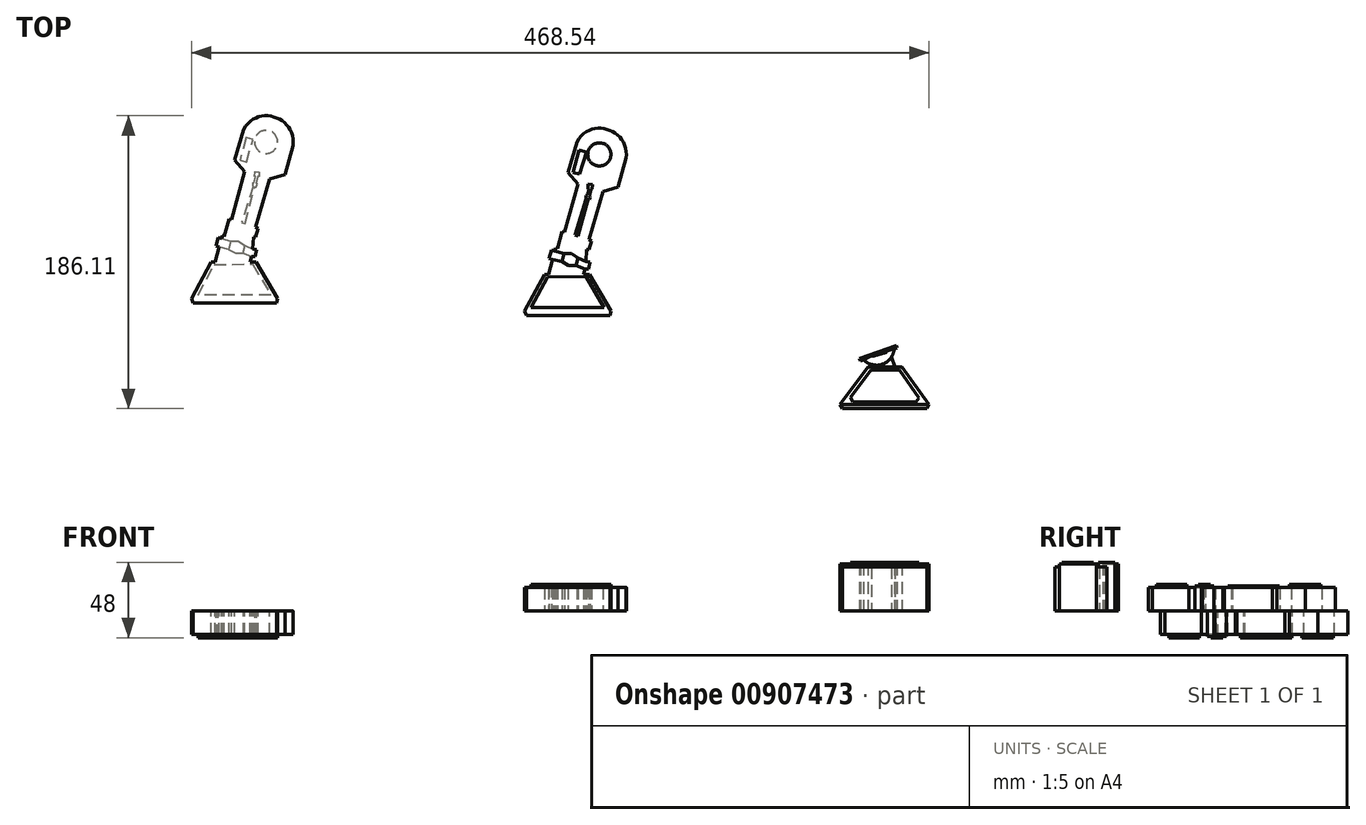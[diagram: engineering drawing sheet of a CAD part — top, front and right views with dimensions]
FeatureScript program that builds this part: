
annotation { "Feature Type Name" : "Feature", "Feature Type Description" : "" }
export const myFeature = defineFeature(function(context is Context, id is Id, definition is map)
    precondition{}
    {
        {
            var Q0;
            Q0=qCreatedBy(makeId("Top.planeOp"),FACE);
            var sketch = newSketch(context, id + "F0", { "sketchPlane" : qUnion([Q0])});
            skLineSegment(sketch, "E0", {"start": v(-482.86, 761.62) * mm, "end": v(-495.39, 738.6) * mm});
            skLineSegment(sketch, "E1", {"start": v(-495.39, 738.6) * mm, "end": v(-494.29, 735.67) * mm});
            skLineSegment(sketch, "E2", {"start": v(-494.29, 735.67) * mm, "end": v(-441.2, 735.67) * mm});
            skLineSegment(sketch, "E3", {"start": v(-441.2, 735.67) * mm, "end": v(-440.55, 738.47) * mm});
            skLineSegment(sketch, "E4", {"start": v(-440.55, 738.47) * mm, "end": v(-454.23, 761.7) * mm});
            skLineSegment(sketch, "E5", {"start": v(-454.23, 761.7) * mm, "end": v(-457.97, 761.7) * mm});
            skLineSegment(sketch, "E6", {"start": v(-457.97, 761.7) * mm, "end": v(-457.1, 765.32) * mm});
            skLineSegment(sketch, "E7", {"start": v(-457.1, 765.32) * mm, "end": v(-454.92, 765.32) * mm});
            skLineSegment(sketch, "E8", {"start": v(-454.92, 765.32) * mm, "end": v(-453.98, 769.58) * mm});
            skLineSegment(sketch, "E9", {"start": v(-453.98, 769.58) * mm, "end": v(-456.42, 770.11) * mm});
            skLineSegment(sketch, "E10", {"start": v(-456.42, 770.11) * mm, "end": v(-456.01, 777.64) * mm});
            skLineSegment(sketch, "E11", {"start": v(-456.01, 777.64) * mm, "end": v(-454.5, 777.56) * mm});
            skLineSegment(sketch, "E12", {"start": v(-454.5, 777.56) * mm, "end": v(-453, 783.11) * mm});
            skLineSegment(sketch, "E13", {"start": v(-453, 783.11) * mm, "end": v(-454.5, 784.13) * mm});
            skLineSegment(sketch, "E14", {"start": v(-454.5, 784.13) * mm, "end": v(-445.55, 814.56) * mm});
            skLineSegment(sketch, "E15", {"start": v(-445.55, 814.56) * mm, "end": v(-436, 817.4) * mm});
            skLineSegment(sketch, "E16", {"start": v(-436, 817.4) * mm, "end": v(-430.92, 835.6) * mm});
            skLineSegment(sketch, "E17", {"start": v(-482.86, 761.62) * mm, "end": v(-480.27, 761.62) * mm});
            skLineSegment(sketch, "E18", {"start": v(-480.27, 761.62) * mm, "end": v(-477.79, 771.15) * mm});
            skLineSegment(sketch, "E19", {"start": v(-477.79, 771.15) * mm, "end": v(-479.74, 771.98) * mm});
            skLineSegment(sketch, "E20", {"start": v(-479.74, 771.98) * mm, "end": v(-478.29, 777.28) * mm});
            skLineSegment(sketch, "E21", {"start": v(-478.29, 777.28) * mm, "end": v(-476.27, 776.72) * mm});
            skLineSegment(sketch, "E22", {"start": v(-476.27, 776.72) * mm, "end": v(-475.8, 778.46) * mm});
            skLineSegment(sketch, "E23", {"start": v(-475.8, 778.46) * mm, "end": v(-474.52, 778.11) * mm});
            skLineSegment(sketch, "E24", {"start": v(-474.52, 778.11) * mm, "end": v(-471.51, 789.04) * mm});
            skLineSegment(sketch, "E25", {"start": v(-471.51, 789.04) * mm, "end": v(-469.92, 788.6) * mm});
            skLineSegment(sketch, "E26", {"start": v(-469.92, 788.6) * mm, "end": v(-461.5, 819.22) * mm});
            skLineSegment(sketch, "E27", {"start": v(-461.5, 819.22) * mm, "end": v(-467.88, 826.48) * mm});
            skLineSegment(sketch, "E28", {"start": v(-467.88, 826.48) * mm, "end": v(-462.18, 846) * mm});
            skFitSpline(sketch, "E29", {"points": [v(-462.18, 846) * mm, v(-430.92, 835.6) * mm], "startDerivative": vector(27.78, 49.97) * mm, "endDerivative": vector(-7.84, -52.92) * mm});
            skCircle(sketch, "E30", {"center": v(-447.9, 838.04) * mm, "radius": 7.37 * mm});
            skLineSegment(sketch, "E31", {"start": v(-460.78, 840.85) * mm, "end": v(-464.5, 826.48) * mm});
            skLineSegment(sketch, "E32", {"start": v(-464.5, 826.48) * mm, "end": v(-460.37, 825.42) * mm});
            skLineSegment(sketch, "E33", {"start": v(-460.37, 825.42) * mm, "end": v(-456.2, 839.69) * mm});
            skLineSegment(sketch, "E34", {"start": v(-456.2, 839.69) * mm, "end": v(-460.78, 840.85) * mm});
            skLineSegment(sketch, "E35", {"start": v(-476.27, 776.72) * mm, "end": v(-470.47, 775.03) * mm});
            skLineSegment(sketch, "E36", {"start": v(-470.47, 775.03) * mm, "end": v(-471.7, 769.86) * mm});
            skLineSegment(sketch, "E37", {"start": v(-471.7, 769.86) * mm, "end": v(-477.79, 771.15) * mm});
            skLineSegment(sketch, "E38", {"start": v(-462.64, 767.48) * mm, "end": v(-457.1, 765.32) * mm});
            skLineSegment(sketch, "E39", {"start": v(-462.64, 767.48) * mm, "end": v(-461.35, 772.18) * mm});
            skLineSegment(sketch, "E40", {"start": v(-461.35, 772.18) * mm, "end": v(-456.42, 770.11) * mm});
            skLineSegment(sketch, "E41", {"start": v(-471.7, 769.86) * mm, "end": v(-467.42, 767.48) * mm});
            skLineSegment(sketch, "E42", {"start": v(-467.42, 767.48) * mm, "end": v(-462.64, 767.48) * mm});
            skLineSegment(sketch, "E43", {"start": v(-470.47, 775.03) * mm, "end": v(-465.57, 775.03) * mm});
            skLineSegment(sketch, "E44", {"start": v(-465.57, 775.03) * mm, "end": v(-461.35, 772.18) * mm});
            skLineSegment(sketch, "E45", {"start": v(-491.4, 740.51) * mm, "end": v(-480.92, 760.24) * mm});
            skLineSegment(sketch, "E46", {"start": v(-480.92, 760.24) * mm, "end": v(-456.42, 760.37) * mm});
            skLineSegment(sketch, "E47", {"start": v(-456.42, 760.37) * mm, "end": v(-444.92, 740.85) * mm});
            skLineSegment(sketch, "E48", {"start": v(-444.92, 740.85) * mm, "end": v(-491.23, 740.85) * mm});
            skLineSegment(sketch, "E49", {"start": v(-463.38, 786.76) * mm, "end": v(-461.3, 786.21) * mm});
            skLineSegment(sketch, "E50", {"start": v(-461.3, 786.21) * mm, "end": v(-455.2, 809.29) * mm});
            skLineSegment(sketch, "E51", {"start": v(-455.2, 809.29) * mm, "end": v(-454.22, 809.29) * mm});
            skLineSegment(sketch, "E52", {"start": v(-454.22, 809.29) * mm, "end": v(-453.74, 810.98) * mm});
            skLineSegment(sketch, "E53", {"start": v(-453.74, 810.98) * mm, "end": v(-456.51, 811.78) * mm});
            skLineSegment(sketch, "E54", {"start": v(-456.51, 811.78) * mm, "end": v(-456.51, 810.19) * mm});
            skLineSegment(sketch, "E55", {"start": v(-456.51, 810.19) * mm, "end": v(-456.28, 809.74) * mm});
            skLineSegment(sketch, "E56", {"start": v(-456.28, 809.74) * mm, "end": v(-463.38, 786.76) * mm});
            skLineSegment(sketch, "E57", {"start": v(-456.51, 811.78) * mm, "end": v(-455.52, 812.18) * mm});
            skLineSegment(sketch, "E58", {"start": v(-455.52, 812.18) * mm, "end": v(-454.5, 816.03) * mm});
            skLineSegment(sketch, "E59", {"start": v(-454.5, 816.03) * mm, "end": v(-455.2, 816.03) * mm});
            skLineSegment(sketch, "E60", {"start": v(-455.2, 816.03) * mm, "end": v(-454.98, 819.08) * mm});
            skLineSegment(sketch, "E61", {"start": v(-454.98, 819.08) * mm, "end": v(-452.27, 818.9) * mm});
            skLineSegment(sketch, "E62", {"start": v(-452.27, 818.9) * mm, "end": v(-452.48, 815.9) * mm});
            skLineSegment(sketch, "E63", {"start": v(-452.48, 815.9) * mm, "end": v(-453.21, 815.95) * mm});
            skLineSegment(sketch, "E64", {"start": v(-453.21, 815.95) * mm, "end": v(-454.11, 811.78) * mm});
            skLineSegment(sketch, "E65", {"start": v(-454.11, 811.78) * mm, "end": v(-453.74, 810.98) * mm});
            skLineSegment(sketch, "E66", {"start": v(-282.7, 708.42) * mm, "end": v(-282, 706.84) * mm});
            skLineSegment(sketch, "E67", {"start": v(-282, 706.84) * mm, "end": v(-275.28, 709.86) * mm});
            skLineSegment(sketch, "E68", {"start": v(-275.28, 709.86) * mm, "end": v(-273.39, 709.86) * mm});
            skLineSegment(sketch, "E69", {"start": v(-273.39, 709.86) * mm, "end": v(-265.97, 712.14) * mm});
            skLineSegment(sketch, "E70", {"start": v(-265.97, 712.14) * mm, "end": v(-265.13, 713.32) * mm});
            skLineSegment(sketch, "E71", {"start": v(-265.13, 713.32) * mm, "end": v(-258.84, 715.15) * mm});
            skLineSegment(sketch, "E72", {"start": v(-258.84, 715.15) * mm, "end": v(-259.3, 716.74) * mm});
            skLineSegment(sketch, "E73", {"start": v(-277.24, 702.88) * mm, "end": v(-255.68, 702.88) * mm});
            skLineSegment(sketch, "E74", {"start": v(-255.68, 702.88) * mm, "end": v(-238.48, 679.32) * mm});
            skLineSegment(sketch, "E75", {"start": v(-238.48, 679.32) * mm, "end": v(-294.96, 679.32) * mm});
            skLineSegment(sketch, "E76", {"start": v(-294.96, 679.32) * mm, "end": v(-277.24, 702.88) * mm});
            skLineSegment(sketch, "E77", {"start": v(-238.48, 679.32) * mm, "end": v(-239.73, 676.51) * mm});
            skLineSegment(sketch, "E78", {"start": v(-239.73, 676.51) * mm, "end": v(-293.64, 676.51) * mm});
            skLineSegment(sketch, "E79", {"start": v(-293.64, 676.51) * mm, "end": v(-294.96, 679.32) * mm});
            skLineSegment(sketch, "E80", {"start": v(-282.7, 708.42) * mm, "end": v(-259.3, 716.74) * mm});
            skLineSegment(sketch, "E81", {"start": v(-286.78, 680.82) * mm, "end": v(-246.77, 680.82) * mm});
            skLineSegment(sketch, "E82", {"start": v(-246.77, 680.82) * mm, "end": v(-244.8, 683.44) * mm});
            skLineSegment(sketch, "E83", {"start": v(-244.8, 683.44) * mm, "end": v(-257.33, 701) * mm});
            skLineSegment(sketch, "E84", {"start": v(-257.33, 701) * mm, "end": v(-275.4, 701) * mm});
            skLineSegment(sketch, "E85", {"start": v(-275.4, 701) * mm, "end": v(-288.38, 683.76) * mm});
            skLineSegment(sketch, "E86", {"start": v(-288.38, 683.76) * mm, "end": v(-286.78, 680.82) * mm});
            skFitSpline(sketch, "E87", {"points": [v(-280.29, 707.6) * mm, v(-260.54, 714.66) * mm], "startDerivative": vector(27.24, -23.78) * mm, "endDerivative": vector(1.93, 24.14) * mm});
            skLineSegment(sketch, "E88", {"start": v(-275.21, 704.64) * mm, "end": v(-275.21, 702.88) * mm});
            skLineSegment(sketch, "E89", {"start": v(-262.42, 709.34) * mm, "end": v(-260.09, 702.88) * mm});
            skLineSegment(sketch, "E90", {"start": v(-694.5, 769.54) * mm, "end": v(-707.02, 746.52) * mm});
            skLineSegment(sketch, "E91", {"start": v(-707.02, 746.52) * mm, "end": v(-705.92, 743.6) * mm});
            skLineSegment(sketch, "E92", {"start": v(-705.92, 743.6) * mm, "end": v(-652.83, 743.6) * mm});
            skLineSegment(sketch, "E93", {"start": v(-652.83, 743.6) * mm, "end": v(-652.18, 746.4) * mm});
            skLineSegment(sketch, "E94", {"start": v(-652.18, 746.4) * mm, "end": v(-665.87, 769.63) * mm});
            skLineSegment(sketch, "E95", {"start": v(-665.87, 769.63) * mm, "end": v(-669.6, 769.63) * mm});
            skLineSegment(sketch, "E96", {"start": v(-669.6, 769.63) * mm, "end": v(-668.73, 773.25) * mm});
            skLineSegment(sketch, "E97", {"start": v(-668.73, 773.25) * mm, "end": v(-666.55, 773.25) * mm});
            skLineSegment(sketch, "E98", {"start": v(-666.55, 773.25) * mm, "end": v(-665.62, 777.5) * mm});
            skLineSegment(sketch, "E99", {"start": v(-665.62, 777.5) * mm, "end": v(-668.05, 778.04) * mm});
            skLineSegment(sketch, "E100", {"start": v(-668.05, 778.04) * mm, "end": v(-667.65, 785.56) * mm});
            skLineSegment(sketch, "E101", {"start": v(-667.65, 785.56) * mm, "end": v(-666.14, 785.48) * mm});
            skLineSegment(sketch, "E102", {"start": v(-666.14, 785.48) * mm, "end": v(-664.63, 791.04) * mm});
            skLineSegment(sketch, "E103", {"start": v(-664.63, 791.04) * mm, "end": v(-666.14, 792.06) * mm});
            skLineSegment(sketch, "E104", {"start": v(-666.14, 792.06) * mm, "end": v(-657.18, 822.49) * mm});
            skLineSegment(sketch, "E105", {"start": v(-657.18, 822.49) * mm, "end": v(-647.62, 825.32) * mm});
            skLineSegment(sketch, "E106", {"start": v(-647.62, 825.32) * mm, "end": v(-642.56, 843.53) * mm});
            skLineSegment(sketch, "E107", {"start": v(-694.5, 769.54) * mm, "end": v(-691.9, 769.54) * mm});
            skLineSegment(sketch, "E108", {"start": v(-691.9, 769.54) * mm, "end": v(-689.42, 779.08) * mm});
            skLineSegment(sketch, "E109", {"start": v(-689.42, 779.08) * mm, "end": v(-691.38, 779.9) * mm});
            skLineSegment(sketch, "E110", {"start": v(-691.38, 779.9) * mm, "end": v(-689.92, 785.2) * mm});
            skLineSegment(sketch, "E111", {"start": v(-689.92, 785.2) * mm, "end": v(-687.9, 784.65) * mm});
            skLineSegment(sketch, "E112", {"start": v(-687.9, 784.65) * mm, "end": v(-687.42, 786.39) * mm});
            skLineSegment(sketch, "E113", {"start": v(-687.42, 786.39) * mm, "end": v(-686.15, 786.04) * mm});
            skLineSegment(sketch, "E114", {"start": v(-686.15, 786.04) * mm, "end": v(-683.14, 796.97) * mm});
            skLineSegment(sketch, "E115", {"start": v(-683.14, 796.97) * mm, "end": v(-681.55, 796.53) * mm});
            skLineSegment(sketch, "E116", {"start": v(-681.55, 796.53) * mm, "end": v(-673.13, 827.14) * mm});
            skLineSegment(sketch, "E117", {"start": v(-673.13, 827.14) * mm, "end": v(-679.51, 834.41) * mm});
            skLineSegment(sketch, "E118", {"start": v(-679.51, 834.41) * mm, "end": v(-673.82, 853.93) * mm});
            skFitSpline(sketch, "E119", {"points": [v(-673.82, 853.93) * mm, v(-642.56, 843.53) * mm], "startDerivative": vector(27.78, 49.97) * mm, "endDerivative": vector(-7.84, -52.92) * mm});
            skCircle(sketch, "E120", {"center": v(-659.54, 845.97) * mm, "radius": 7.37 * mm});
            skLineSegment(sketch, "E121", {"start": v(-672.41, 848.78) * mm, "end": v(-676.12, 834.41) * mm});
            skLineSegment(sketch, "E122", {"start": v(-676.12, 834.41) * mm, "end": v(-672, 833.35) * mm});
            skLineSegment(sketch, "E123", {"start": v(-672, 833.35) * mm, "end": v(-667.84, 847.61) * mm});
            skLineSegment(sketch, "E124", {"start": v(-667.84, 847.61) * mm, "end": v(-672.41, 848.78) * mm});
            skLineSegment(sketch, "E125", {"start": v(-687.9, 784.65) * mm, "end": v(-682.1, 782.96) * mm});
            skLineSegment(sketch, "E126", {"start": v(-682.1, 782.96) * mm, "end": v(-683.34, 777.78) * mm});
            skLineSegment(sketch, "E127", {"start": v(-683.34, 777.78) * mm, "end": v(-689.42, 779.08) * mm});
            skLineSegment(sketch, "E128", {"start": v(-674.27, 775.4) * mm, "end": v(-668.73, 773.25) * mm});
            skLineSegment(sketch, "E129", {"start": v(-674.27, 775.4) * mm, "end": v(-672.98, 780.1) * mm});
            skLineSegment(sketch, "E130", {"start": v(-672.98, 780.1) * mm, "end": v(-668.05, 778.04) * mm});
            skLineSegment(sketch, "E131", {"start": v(-683.34, 777.78) * mm, "end": v(-679.06, 775.4) * mm});
            skLineSegment(sketch, "E132", {"start": v(-679.06, 775.4) * mm, "end": v(-674.27, 775.4) * mm});
            skLineSegment(sketch, "E133", {"start": v(-682.1, 782.96) * mm, "end": v(-677.2, 782.96) * mm});
            skLineSegment(sketch, "E134", {"start": v(-677.2, 782.96) * mm, "end": v(-672.98, 780.1) * mm});
            skLineSegment(sketch, "E135", {"start": v(-703.04, 748.44) * mm, "end": v(-692.56, 768.17) * mm});
            skLineSegment(sketch, "E136", {"start": v(-692.56, 768.17) * mm, "end": v(-668.05, 768.3) * mm});
            skLineSegment(sketch, "E137", {"start": v(-668.05, 768.3) * mm, "end": v(-656.55, 748.78) * mm});
            skLineSegment(sketch, "E138", {"start": v(-656.55, 748.78) * mm, "end": v(-702.86, 748.78) * mm});
            skLineSegment(sketch, "E139", {"start": v(-675, 794.69) * mm, "end": v(-672.93, 794.14) * mm});
            skLineSegment(sketch, "E140", {"start": v(-672.93, 794.14) * mm, "end": v(-666.83, 817.22) * mm});
            skLineSegment(sketch, "E141", {"start": v(-666.83, 817.22) * mm, "end": v(-665.86, 817.22) * mm});
            skLineSegment(sketch, "E142", {"start": v(-665.86, 817.22) * mm, "end": v(-665.37, 818.9) * mm});
            skLineSegment(sketch, "E143", {"start": v(-665.37, 818.9) * mm, "end": v(-668.15, 819.7) * mm});
            skLineSegment(sketch, "E144", {"start": v(-668.15, 819.7) * mm, "end": v(-668.15, 818.11) * mm});
            skLineSegment(sketch, "E145", {"start": v(-668.15, 818.11) * mm, "end": v(-667.92, 817.67) * mm});
            skLineSegment(sketch, "E146", {"start": v(-667.92, 817.67) * mm, "end": v(-675, 794.69) * mm});
            skLineSegment(sketch, "E147", {"start": v(-668.15, 819.7) * mm, "end": v(-667.16, 820.11) * mm});
            skLineSegment(sketch, "E148", {"start": v(-667.16, 820.11) * mm, "end": v(-666.14, 823.96) * mm});
            skLineSegment(sketch, "E149", {"start": v(-666.14, 823.96) * mm, "end": v(-666.83, 823.96) * mm});
            skLineSegment(sketch, "E150", {"start": v(-666.83, 823.96) * mm, "end": v(-666.62, 827.01) * mm});
            skLineSegment(sketch, "E151", {"start": v(-666.62, 827.01) * mm, "end": v(-663.9, 826.83) * mm});
            skLineSegment(sketch, "E152", {"start": v(-663.9, 826.83) * mm, "end": v(-664.11, 823.83) * mm});
            skLineSegment(sketch, "E153", {"start": v(-664.11, 823.83) * mm, "end": v(-664.85, 823.88) * mm});
            skLineSegment(sketch, "E154", {"start": v(-664.85, 823.88) * mm, "end": v(-665.74, 819.7) * mm});
            skLineSegment(sketch, "E155", {"start": v(-665.74, 819.7) * mm, "end": v(-665.37, 818.9) * mm});
            skSolve(sketch);
        }
        {
            var Q0;
            Q0=makeQuery(id+"F0.imprint","IMPRINT",FACE,{"disambiguationData":[TD([[makeQuery(id+"F0.imprint","IMPRINT",EDGE,{"derivedFrom":sQuery(id+"F0.wireOp",EDGE,"E0")}),1.0]])]});
            var Q1;
            Q1=makeQuery(id+"F0.imprint","IMPRINT",FACE,{"disambiguationData":[TD([[makeQuery(id+"F0.imprint","IMPRINT",EDGE,{"derivedFrom":sQuery(id+"F0.wireOp",EDGE,"E10")}),1.0]])]});
            extrude(context, id + "F1", {"entities" : qUnion([Q0, Q1]), "depth" : 15 * mm, "offsetDistance" : 25 * mm});
        }
        {
            var Q0;
            {var subQ0=sQuery(id+"F0.wireOp",EDGE,"E46");Q0=makeQuery(id+"F0.imprint","IMPRINT",FACE,{"disambiguationData":[TD([[makeQuery(id+"F0.imprint","IMPRINT",EDGE,{"derivedFrom":subQ0}),-1.0]])]});}
            var Q1;
            Q1=makeQuery(id+"F0.imprint","IMPRINT",FACE,{"disambiguationData":[TD([[makeQuery(id+"F0.imprint","IMPRINT",EDGE,{"derivedFrom":sQuery(id+"F0.wireOp",EDGE,"E36")}),1.0]])]});
            var Q2;
            Q2=makeQuery(id+"F0.imprint","IMPRINT",FACE,{"disambiguationData":[TD([[makeQuery(id+"F0.imprint","IMPRINT",EDGE,{"derivedFrom":sQuery(id+"F0.wireOp",EDGE,"E30")}),1.0]])]});
            var Q3;
            Q3=makeQuery(id+"F0.imprint","IMPRINT",FACE,{"disambiguationData":[TD([[makeQuery(id+"F0.imprint","IMPRINT",EDGE,{"derivedFrom":sQuery(id+"F0.wireOp",EDGE,"E31")}),1.0]])]});
            extrude(context, id + "F2", {"entities" : qUnion([Q0, Q1, Q2, Q3]), "operationType" : NewBodyOperationType.ADD, "depth" : 17 * mm, "offsetDistance" : 25 * mm});
        }
        {
            var Q0;
            Q0=makeQuery(id+"F0.imprint","IMPRINT",FACE,{"disambiguationData":[TD([[makeQuery(id+"F0.imprint","IMPRINT",EDGE,{"derivedFrom":sQuery(id+"F0.wireOp",EDGE,"E19")}),-1.0]])]});
            var Q1;
            Q1=makeQuery(id+"F0.imprint","IMPRINT",FACE,{"disambiguationData":[TD([[makeQuery(id+"F0.imprint","IMPRINT",EDGE,{"derivedFrom":sQuery(id+"F0.wireOp",EDGE,"E7")}),1.0]])]});
            var Q2;
            Q2=makeQuery(id+"F0.imprint","IMPRINT",FACE,{"disambiguationData":[TD([[makeQuery(id+"F0.imprint","IMPRINT",EDGE,{"derivedFrom":sQuery(id+"F0.wireOp",EDGE,"E49")}),1.0]])]});
            var Q3;
            Q3=makeQuery(id+"F0.imprint","IMPRINT",FACE,{"disambiguationData":[TD([[makeQuery(id+"F0.imprint","IMPRINT",EDGE,{"derivedFrom":sQuery(id+"F0.wireOp",EDGE,"E53")}),-1.0]])]});
            extrude(context, id + "F3", {"entities" : qUnion([Q0, Q1, Q2, Q3]), "operationType" : NewBodyOperationType.ADD, "depth" : 16 * mm, "offsetDistance" : 25 * mm});
        }
        {
            var Q0;
            Q0=makeQuery(id+"F0.imprint","IMPRINT",FACE,{"disambiguationData":[TD([[makeQuery(id+"F0.imprint","IMPRINT",EDGE,{"derivedFrom":sQuery(id+"F0.wireOp",EDGE,"E81")}),1.0]])]});
            var Q1;
            {var subQ1=sQuery(id+"F0.wireOp",EDGE,"E68");Q1=makeQuery(id+"F0.imprint","IMPRINT",FACE,{"disambiguationData":[TD([[makeQuery(id+"F0.imprint","IMPRINT",EDGE,{"derivedFrom":subQ1}),-1.0]])]});}
            extrude(context, id + "F4", {"entities" : qUnion([Q0, Q1]), "depth" : 31 * mm, "offsetDistance" : 25 * mm});
        }
        {
            var Q0;
            {var subQ4=sQuery(id+"F0.wireOp",EDGE,"E74");Q0=makeQuery(id+"F0.imprint","IMPRINT",FACE,{"disambiguationData":[TD([[makeQuery(id+"F0.imprint","IMPRINT",EDGE,{"derivedFrom":subQ4}),-1.0]])]});}
            var Q1;
            {var subQ4=sQuery(id+"F0.wireOp",EDGE,"E66");Q1=makeQuery(id+"F0.imprint","IMPRINT",FACE,{"disambiguationData":[TD([[makeQuery(id+"F0.imprint","IMPRINT",EDGE,{"derivedFrom":subQ4}),1.0]])]});}
            extrude(context, id + "F5", {"entities" : qUnion([Q0, Q1]), "operationType" : NewBodyOperationType.ADD, "depth" : 30 * mm, "offsetDistance" : 25 * mm});
        }
        {
            var Q0;
            {var subQ0=sQuery(id+"F0.wireOp",EDGE,"E88");Q0=makeQuery(id+"F0.imprint","IMPRINT",FACE,{"disambiguationData":[TD([[makeQuery(id+"F0.imprint","IMPRINT",EDGE,{"derivedFrom":subQ0}),1.0]])]});}
            var Q1;
            Q1=makeQuery(id+"F0.imprint","IMPRINT",FACE,{"disambiguationData":[TD([[makeQuery(id+"F0.imprint","IMPRINT",EDGE,{"derivedFrom":sQuery(id+"F0.wireOp",EDGE,"E75")}),1.0]])]});
            extrude(context, id + "F6", {"entities" : qUnion([Q0, Q1]), "operationType" : NewBodyOperationType.ADD, "depth" : 28 * mm, "offsetDistance" : 25 * mm});
        }
        {
            var Q0;
            Q0=makeQuery(id+"F0.imprint","IMPRINT",FACE,{"disambiguationData":[TD([[makeQuery(id+"F0.imprint","IMPRINT",EDGE,{"derivedFrom":sQuery(id+"F0.wireOp",EDGE,"E90")}),1.0]])]});
            var Q1;
            Q1=makeQuery(id+"F0.imprint","IMPRINT",FACE,{"disambiguationData":[TD([[makeQuery(id+"F0.imprint","IMPRINT",EDGE,{"derivedFrom":sQuery(id+"F0.wireOp",EDGE,"E100")}),1.0]])]});
            extrude(context, id + "F7", {"entities" : qUnion([Q0, Q1]), "oppositeDirection" : true, "depth" : 15 * mm, "offsetDistance" : 25 * mm});
        }
        {
            var Q0;
            Q0=makeQuery(id+"F0.imprint","IMPRINT",FACE,{"disambiguationData":[TD([[makeQuery(id+"F0.imprint","IMPRINT",EDGE,{"derivedFrom":sQuery(id+"F0.wireOp",EDGE,"E120")}),1.0]])]});
            var Q1;
            Q1=makeQuery(id+"F0.imprint","IMPRINT",FACE,{"disambiguationData":[TD([[makeQuery(id+"F0.imprint","IMPRINT",EDGE,{"derivedFrom":sQuery(id+"F0.wireOp",EDGE,"E121")}),1.0]])]});
            var Q2;
            Q2=makeQuery(id+"F0.imprint","IMPRINT",FACE,{"disambiguationData":[TD([[makeQuery(id+"F0.imprint","IMPRINT",EDGE,{"derivedFrom":sQuery(id+"F0.wireOp",EDGE,"E126")}),1.0]])]});
            var Q3;
            {var subQ0=sQuery(id+"F0.wireOp",EDGE,"E136");Q3=makeQuery(id+"F0.imprint","IMPRINT",FACE,{"disambiguationData":[TD([[makeQuery(id+"F0.imprint","IMPRINT",EDGE,{"derivedFrom":subQ0}),-1.0]])]});}
            var Q4;
            Q4=makeQuery(id+"F0.imprint","IMPRINT",FACE,{"disambiguationData":[TD([[makeQuery(id+"F0.imprint","IMPRINT",EDGE,{"derivedFrom":sQuery(id+"F0.wireOp",EDGE,"E139")}),1.0]])]});
            var Q5;
            Q5=makeQuery(id+"F0.imprint","IMPRINT",FACE,{"disambiguationData":[TD([[makeQuery(id+"F0.imprint","IMPRINT",EDGE,{"derivedFrom":sQuery(id+"F0.wireOp",EDGE,"E143")}),-1.0]])]});
            extrude(context, id + "F8", {"entities" : qUnion([Q0, Q1, Q2, Q3, Q4, Q5]), "operationType" : NewBodyOperationType.ADD, "oppositeDirection" : true, "depth" : 17 * mm, "offsetDistance" : 25 * mm});
        }
        {
            var Q0;
            Q0=makeQuery(id+"F0.imprint","IMPRINT",FACE,{"disambiguationData":[TD([[makeQuery(id+"F0.imprint","IMPRINT",EDGE,{"derivedFrom":sQuery(id+"F0.wireOp",EDGE,"E109")}),-1.0]])]});
            var Q1;
            Q1=makeQuery(id+"F0.imprint","IMPRINT",FACE,{"disambiguationData":[TD([[makeQuery(id+"F0.imprint","IMPRINT",EDGE,{"derivedFrom":sQuery(id+"F0.wireOp",EDGE,"E97")}),1.0]])]});
            extrude(context, id + "F9", {"entities" : qUnion([Q0, Q1]), "operationType" : NewBodyOperationType.ADD, "oppositeDirection" : true, "depth" : 16 * mm, "offsetDistance" : 25 * mm});
        }
    });
